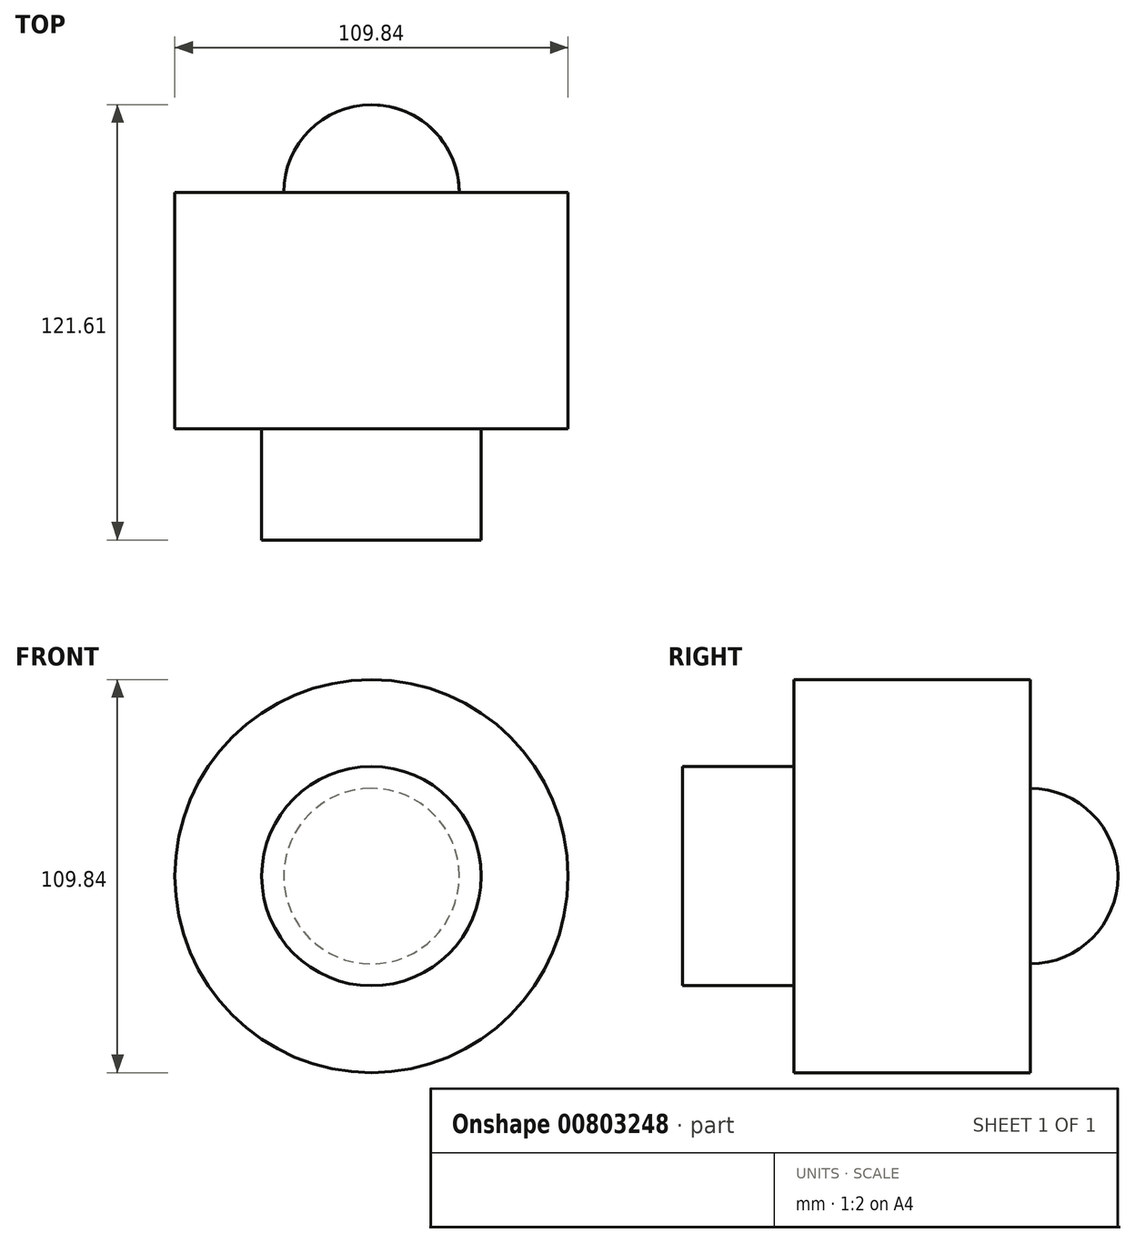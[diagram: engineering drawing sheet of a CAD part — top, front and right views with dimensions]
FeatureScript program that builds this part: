
annotation { "Feature Type Name" : "Feature", "Feature Type Description" : "" }
export const myFeature = defineFeature(function(context is Context, id is Id, definition is map)
    precondition{}
    {
        {
            var Q0;
            Q0=qCreatedBy(makeId("Top.planeOp"),FACE);
            var sketch = newSketch(context, id + "F0", { "sketchPlane" : qUnion([Q0])});
            skLineSegment(sketch, "E0", {"start": v(0, 74.82) * mm, "end": v(0, -74.82) * mm, "construction": true});
            skLineSegment(sketch, "E1.bottom", {"start": v(24.52, 42.17) * mm, "end": v(54.92, 42.17) * mm});
            skLineSegment(sketch, "E1.top", {"start": v(30.64, -23.83) * mm, "end": v(54.92, -23.83) * mm});
            skLineSegment(sketch, "E1.left", {"start": v(0, 42.17) * mm, "end": v(0, -23.83) * mm});
            skLineSegment(sketch, "E1.right", {"start": v(54.92, 42.17) * mm, "end": v(54.92, -23.83) * mm});
            skLineSegment(sketch, "E2.top", {"start": v(0, -54.92) * mm, "end": v(30.64, -54.92) * mm});
            skLineSegment(sketch, "E2.right", {"start": v(30.64, -23.83) * mm, "end": v(30.64, -54.92) * mm});
            skArc(sketch, "E3", {"start": v(24.52, 42.17) * mm, "mid": v(17.34, 59.5) * mm, "end": v(0, 66.7) * mm});
            skLineSegment(sketch, "E4", {"start": v(0, 66.7) * mm, "end": v(0, -54.92) * mm});
            skSolve(sketch);
        }
        {
            var Q0;
            Q0=makeQuery(id+"F0.imprint","IMPRINT",FACE,{"disambiguationData":[TD([[makeQuery(id+"F0.imprint","IMPRINT",EDGE,{"derivedFrom":sQuery(id+"F0.wireOp",EDGE,"E1.bottom")}),-1.0]])]});
            var Q1;
            Q1=sQuery(id+"F0.wireOp",EDGE,"E4");
            revolve(context, id + "F1", {"surfaceOperationType" : NewSurfaceOperationType.NEW, "entities" : qUnion([Q0]), "axis" : qUnion([Q1]), "revolveType" : RevolveType.FULL});
        }
    });
